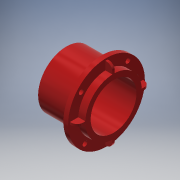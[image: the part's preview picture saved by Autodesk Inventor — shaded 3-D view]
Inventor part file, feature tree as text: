
AUTODESK INVENTOR PART (.ipt)
format: ipt  version: 2019 (Build 230136000, 136)  size: 846,848 bytes
history: native  units: mm
features: sketch x33, extrude x32, projected_geometry x12, fillet x5, other x3
ambient origin geometry x8: Origin, YZ Plane, XZ Plane, XY Plane, X Axis, Y Axis, Z Axis, Center Point
bodies: Body1 (feature_tree), Body2 (feature_tree)
feature tree (85):
  other  "Твердое тело1"
  other  "0ae4c1a17e304db4a8c8e39318f74883.stl"
  extrude  "Выдавливание1"  Depth=3.0mm TaperAngle=0.0deg
  extrude  "Выдавливание2"  Depth=43.0mm
  extrude  "Выдавливание3"  Depth=25.0mm TaperAngle=0.0deg
  extrude  "Выдавливание4"  Depth=20.0mm
  extrude  "Выдавливание5"  Depth=20.0mm
  extrude  "Выдавливание6"  Depth=50.0mm TaperAngle=0.0deg
  extrude  "Выдавливание7"  Depth=34.0mm
  extrude  "Выдавливание8"  Depth=2.0mm
  extrude  "Выдавливание9"  Depth=2.0mm
  extrude  "Выдавливание10"  Depth=1.0mm TaperAngle=0.0deg
  sketch  "Эскиз15"
  sketch  "Эскиз16"
  extrude  "Выдавливание11"  Depth=25.0mm TaperAngle=0.0deg
  extrude  "Выдавливание12"  Depth=4.0mm
  extrude  "Выдавливание13"  Depth=4.0mm
  extrude  "Выдавливание14"  Depth=4.0mm
  extrude  "Выдавливание15"  Depth=4.0mm
  extrude  "Выдавливание16"  Depth=4.5mm
  fillet  "Сопряжение1"  Radius=4.5mm
  fillet  "Сопряжение2"  Radius=4.5mm
  extrude  "Выдавливание17"  Depth=4.5mm
  extrude  "Выдавливание18"  Depth=25.0mm TaperAngle=0.0deg
  extrude  "Выдавливание19"  Depth=7.2mm
  extrude  "Выдавливание20"  Depth=7.2mm
  extrude  "Выдавливание21"  Depth=7.2mm
  extrude  "Выдавливание22"  Depth=7.2mm
  fillet  "Сопряжение3"  Radius=2.0mm
  extrude  "Выдавливание23"  Depth=15.0mm TaperAngle=0.0deg
  extrude  "Выдавливание24"  Depth=15.0mm
  extrude  "Выдавливание25"  Depth=3.0mm
  extrude  "Выдавливание26"  Depth=13.663525mm
  extrude  "Выдавливание27"  Depth=30.32705mm
  extrude  "Выдавливание28"  Depth=8.5mm TaperAngle=0.0deg
  fillet  "Сопряжение4"  Radius=8.5mm
  extrude  "Выдавливание29"  Depth=38.8mm
  extrude  "Выдавливание30"  Depth=22.0mm TaperAngle=0.0deg
  extrude  "Выдавливание31"  Depth=25.0mm TaperAngle=0.0deg
  extrude  "Выдавливание32"  Depth=10.0mm TaperAngle=0.0deg
  fillet  "Сопряжение5"  Radius=3.5mm
  sketch  "Эскиз2"
  sketch  "Эскиз3"
  sketch  "Эскиз5"
  sketch  "Эскиз6"
  projected_geometry  "Спроецированная петля1"
  sketch  "Эскиз8"
  sketch  "Эскиз9"
  projected_geometry  "Спроецированная петля3"
  sketch  "Эскиз11"
  sketch  "Эскиз12"
  projected_geometry  "Спроецированная петля4"
  sketch  "Эскиз13"
  sketch  "Эскиз14"
  sketch  "Эскиз17"
  sketch  "Эскиз18"
  projected_geometry  "Спроецированная петля5"
  sketch  "Эскиз19"
  projected_geometry  "Спроецированная петля6"
  projected_geometry  "Спроецированная петля7"
  sketch  "Эскиз20"
  projected_geometry  "Спроецированная петля8"
  sketch  "Эскиз21"
  projected_geometry  "Спроецированная петля9"
  sketch  "Эскиз22"
  projected_geometry  "Спроецированная петля10"
  sketch  "Эскиз23"
  sketch  "Эскиз24"
  sketch  "Эскиз25"
  sketch  "Эскиз26"
  sketch  "Эскиз27"
  sketch  "Эскиз28"
  sketch  "Эскиз29"
  sketch  "Эскиз30"
  sketch  "Эскиз31"
  projected_geometry  "Спроецированная петля11"
  sketch  "Эскиз32"
  projected_geometry  "Спроецированная петля12"
  sketch  "Эскиз33"
  sketch  "Эскиз34"
  sketch  "Эскиз35"
  projected_geometry  "Спроецированная петля13"
  sketch  "Эскиз36"
  sketch  "Эскиз37"
  other  "ЭлементСетки1"
